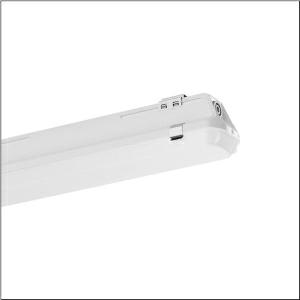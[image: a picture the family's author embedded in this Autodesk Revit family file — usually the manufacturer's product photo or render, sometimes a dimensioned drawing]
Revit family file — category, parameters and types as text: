
# Revit family: monsun_r__11_51fp22mp4b0q_0e64
name_source: partatom
category: Lighting Fixtures
units: mm (PartAtom-declared; Revit-internal decimal feet)

## family parameters
Cut with Voids When Loaded = No
Host = Face
Light Source = No
Part Type = Normal
Room Calculation Point = No
Round Connector Dimension = Use Diameter
Shared = No

## types (1)
- --- (1 x LED, 10520 lm, 66.2 W, 4000K)
    Apparent Load = 66 VA
    CIE Flux Codes = 49 78 94 96 100
    Color Rendering = 80
    Color Temperature = 4000K
    Default Elevation = 1800 mm
    Description = Monsun® 11, damp-proof luminaire, chain hanger, primary light control with lens, primary optical cover: enclosure, of PC, light emission: direct distribution, primary light characteristic: symmetric, installation type: suspended mounting, surface-mounted, horizontal mounting, vertical mounting, LED, rated luminous flux: 10.520lm, luminous efficacy: 159lm/W, light colour: 840, colour temperature: 4000K, control gear: ECG, with terminal, 3-pole, max. 2.5mm², mains connection: 220..240V, AC, 50/60Hz, rated input power: 66W, luminaire housing, of glass-fibre reinforced polyester, uncoated, bright grey, incl. chain hanger, length: 1.590mm, width: 90mm, height: 88mm, clip for enclosure, of stainless steel (V2A), ceiling mounting element, of stainless steel (V2A), chain hanger, of stainless steel (V2A), protection rating (complete): IP66, insulation class (complete): insulation class I (protective earthing), certification: CE, ENEC, VDE, UKCA, protection symbol: D, impact resistance: IK08, permissible operating ambient temperature: -35..+35°C, standard: EN 50419, EN 60598-2-1, no direct snow, no direct sun, no direct rain, for indoor or canopied outdoor use, corresponds to IFS (International Featured Standards) requirements for safety and quality in the food industry, contact your sales advisor before using the luminaires in applications with unclear chemical exposure, large temperature fluctuations or condensation-forming humidity, LABS conformity tested according to VDMA 24364:2018-05, packaging unit: 1 piece
    Height = 89 mm
    Lamp = 1 x LED
    Lamp Light Flux = 10520 lm
    Lamp Power = 66.2 W
    Lamp count = 1
    Length = 1590 mm
    Luminous efficacy = 159 lm/W
    Manufacturer = Siteco
    ModVariant = No
    Model = 51FP22MP4B0Q
    Mounting Place = Ceiling
    Mounting Type = Surface mounted
    Number of Poles = 1
    OnlyDefault = Yes
    Power Factor = 1
    Product Name = Monsun® 11
    Product group = damp-proof luminaire
    ProductGroupID = 300
    Protection Class = Protection class I
    Protection Degree = IP 66
    RLX_Detail_Level = 1
    RLX_Emergency_Light_Flux = 0 lm
    RLX_Emergency_Type = 0
    RLX_Emergency_Type_DB = No
    RlxData = <blob elided: 89681 chars, md5=060b7cac>
    Socket = socket
    Standby Power = 0 W
    System Light Flux = 10520 lm
    System Power = 66 W
    Type Comments = factory setting: luminous flux: 100 % | (A | C | E) | 155 mA
    Type Image = l_1004748.jpg
    URL = http://relux.com
    VarID = @adj_140669
    Voltage = 0 V
    Weight = 0.00 kg
    Width = 90 mm

## geometry (parser evidence)
native form markers: Blend x4, Sweep x11
no freeform markers — native parametric forms only
